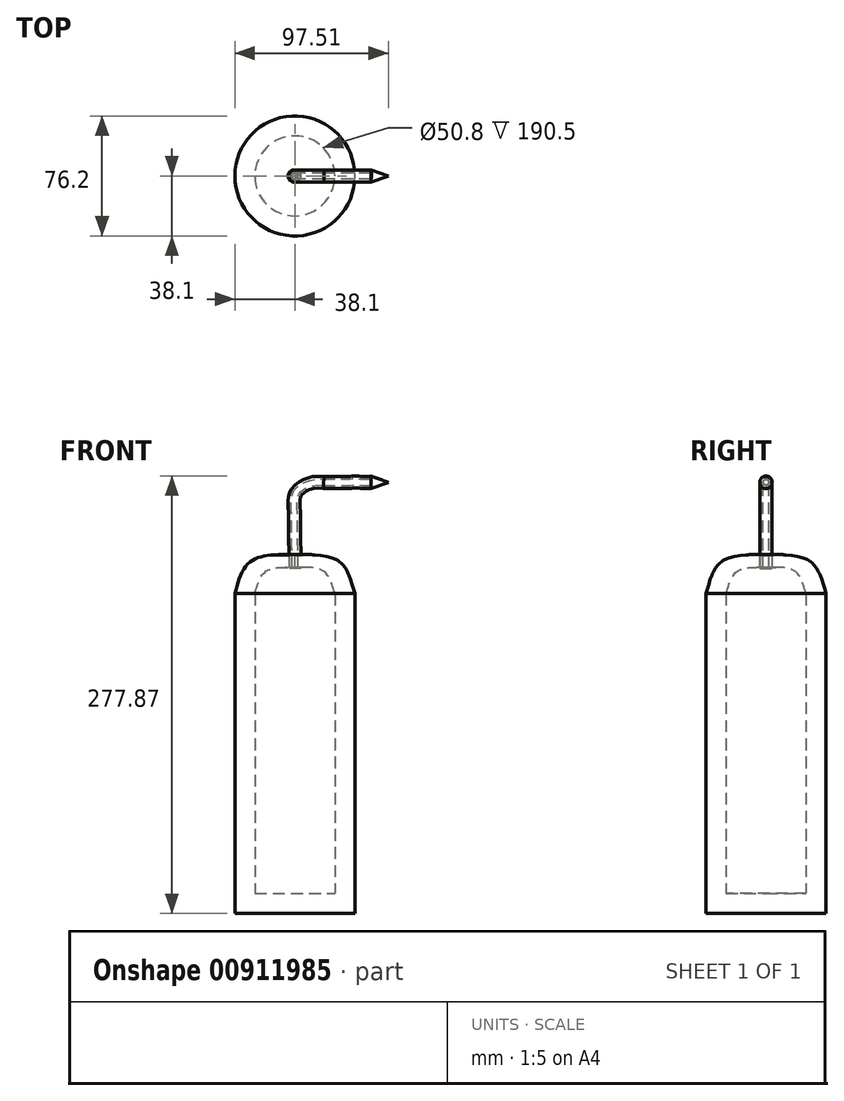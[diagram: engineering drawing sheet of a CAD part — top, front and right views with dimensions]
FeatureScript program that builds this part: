
annotation { "Feature Type Name" : "Feature", "Feature Type Description" : "" }
export const myFeature = defineFeature(function(context is Context, id is Id, definition is map)
    precondition{}
    {
        {
            var Q0;
            Q0=qCreatedBy(makeId("Front.planeOp"),FACE);
            var sketch = newSketch(context, id + "F0", { "sketchPlane" : qUnion([Q0])});
            skLineSegment(sketch, "E0.bottom", {"start": v(-34.29, 171.4) * mm, "end": v(-21.59, 171.4) * mm});
            skLineSegment(sketch, "E0.top", {"start": v(-34.29, -31.8) * mm, "end": v(-21.59, -31.8) * mm});
            skLineSegment(sketch, "E0.left", {"start": v(-34.29, 171.4) * mm, "end": v(-34.29, -31.8) * mm});
            skLineSegment(sketch, "E0.right", {"start": v(-21.59, 171.4) * mm, "end": v(-21.59, -31.8) * mm});
            skLineSegment(sketch, "E1.bottom", {"start": v(-21.59, -19.1) * mm, "end": v(3.81, -19.1) * mm});
            skLineSegment(sketch, "E1.top", {"start": v(-21.59, -31.8) * mm, "end": v(3.81, -31.8) * mm});
            skLineSegment(sketch, "E1.left", {"start": v(-21.59, -19.1) * mm, "end": v(-21.59, -31.8) * mm});
            skLineSegment(sketch, "E1.right", {"start": v(3.81, -19.1) * mm, "end": v(3.81, -31.8) * mm});
            skLineSegment(sketch, "E2", {"start": v(3.81, -19.1) * mm, "end": v(3.81, 201.68) * mm, "construction": true});
            skLineSegment(sketch, "E3", {"start": v(-21.59, 171.4) * mm, "end": v(3.81, 171.4) * mm, "construction": true});
            skLineSegment(sketch, "E4", {"start": v(0, 171.4) * mm, "end": v(0, 200.93) * mm, "construction": true});
            skLineSegment(sketch, "E5", {"start": v(0, 171.4) * mm, "end": v(3.81, 171.4) * mm, "construction": true});
            skFitSpline(sketch, "E6", {"points": [v(-21.59, 171.4) * mm, v(-14.67, 185.45) * mm, v(0, 188.03) * mm], "startDerivative": vector(9.61, 33.45) * mm, "endDerivative": vector(33.67, -0.32) * mm});
            skFitSpline(sketch, "E7", {"points": [v(-34.29, 171.4) * mm, v(-26.66, 189.62) * mm, v(-14.36, 195.48) * mm, v(0, 195.64) * mm], "startDerivative": vector(14.37, 54.55) * mm, "endDerivative": vector(38.3, -6.03) * mm});
            skLineSegment(sketch, "E8", {"start": v(0, 195.64) * mm, "end": v(0, 188.03) * mm});
            skSolve(sketch);
        }
        {
            var Q0;
            Q0=qCreatedBy(makeId("Front.planeOp"),FACE);
            var sketch = newSketch(context, id + "F1", { "sketchPlane" : qUnion([Q0])});
            skFitSpline(sketch, "E9", {"points": [v(3.99, 187.38) * mm, v(3.66, 212.53) * mm, v(3.53, 222.24) * mm, v(3.38, 230.4) * mm, v(5.65, 236.87) * mm, v(22.13, 242.12) * mm], "startDerivative": vector(-1.45, 96.27) * mm, "endDerivative": vector(99.72, -10.55) * mm});
            skFitSpline(sketch, "E10", {"points": [v(22.13, 242.12) * mm, v(38.2, 242.12) * mm, v(48.37, 242.12) * mm, v(52.5, 242.12) * mm], "startDerivative": vector(40.87, -1.49) * mm, "endDerivative": vector(16.8, 0) * mm});
            skFitSpline(sketch, "E11", {"points": [v(52.5, 242.12) * mm, v(58, 242.12) * mm], "startDerivative": vector(5.5, 0) * mm, "endDerivative": vector(5.5, 0) * mm});
            skLineSegment(sketch, "E12", {"start": v(58, 242.12) * mm, "end": v(58, -57.55) * mm, "construction": true});
            skSolve(sketch);
        }
        {
            var Q0;
            Q0=sQuery(id+"F1.wireOp",VERTEX,"E9.start");
            var Q1;
            Q1=sQuery(id+"F1.wireOp",EDGE,"E9");
            cPlane(context, id + "F2", {"entities" : qUnion([Q0, Q1]), "cplaneType" : CPlaneType.CURVE_POINT, "offset" : 25.4 * mm, "width" : 152.4 * mm, "height" : 152.4 * mm});
        }
        {
            var Q0;
            Q0=qCreatedBy(id+"F2.planeOp",FACE);
            var sketch = newSketch(context, id + "F3", { "sketchPlane" : qUnion([Q0])});
            skCircle(sketch, "E13", {"center": v(6.8, 0) * mm, "radius": 3.8 * mm});
            skCircle(sketch, "E14", {"center": v(6.8, 0) * mm, "radius": 1.9 * mm});
            skSolve(sketch);
        }
        {
            var Q0;
            {var subQ2=sQuery(id+"F0.wireOp",EDGE,"E0.bottom");var subQ3=sQuery(id+"F0.wireOp",EDGE,"E1.bottom");var subQ6=makeQuery(id+"F0.imprint","IMPRINT",EDGE,{"derivedFrom":subQ2});Q0=qUnion([makeQuery(id+"F0.imprint","IMPRINT",FACE,{"disambiguationData":[TD([[subQ6,1.0]])]}),makeQuery(id+"F0.imprint","IMPRINT",FACE,{"disambiguationData":[TD([[makeQuery(id+"F0.imprint","IMPRINT",EDGE,{"derivedFrom":subQ3}),-1.0]])]}),makeQuery(id+"F0.imprint","IMPRINT",FACE,{"disambiguationData":[TD([[subQ6,-1.0]])]})]);}
            var Q1;
            Q1=sQuery(id+"F0.wireOp",EDGE,"E2");
            revolve(context, id + "F4", {"surfaceOperationType" : NewSurfaceOperationType.NEW, "entities" : qUnion([Q0]), "axis" : qUnion([Q1]), "revolveType" : RevolveType.FULL});
        }
        {
            var Q0;
            Q0 = qSketchRegion(id + "F3", true);
            var Q1;
            Q1=sQuery(id+"F1.wireOp",EDGE,"E9");
            var Q2;
            Q2=sQuery(id+"F1.wireOp",EDGE,"E10");
            sweep(context, id + "F5", {"operationType" : NewBodyOperationType.ADD, "profiles" : qUnion([Q0]), "path" : qUnion([Q1, Q2])});
        }
        {
            var Q0;
            Q0=qCreatedBy(makeId("Top.planeOp"),FACE);
            cPlane(context, id + "F6", {"entities" : qUnion([Q0]), "cplaneType" : CPlaneType.OFFSET, "offset" : 242.06 * mm, "width" : 152.4 * mm, "height" : 152.4 * mm});
        }
        {
            var Q0;
            Q0=qCreatedBy(id+"F6.planeOp",FACE);
            var sketch = newSketch(context, id + "F7", { "sketchPlane" : qUnion([Q0])});
            skLineSegment(sketch, "E15", {"start": v(52.2, -0.05) * mm, "end": v(63.22, -0.05) * mm});
            skLineSegment(sketch, "E16", {"start": v(52.2, -0.05) * mm, "end": v(52.2, -4) * mm});
            skLineSegment(sketch, "E17", {"start": v(52.2, -4) * mm, "end": v(63.22, -0.05) * mm});
            skSolve(sketch);
        }
        {
            var Q0;
            Q0 = qSketchRegion(id + "F7", true);
            var Q1;
            Q1=sQuery(id+"F7.wireOp",EDGE,"E15");
            revolve(context, id + "F8", {"operationType" : NewBodyOperationType.ADD, "surfaceOperationType" : NewSurfaceOperationType.NEW, "entities" : qUnion([Q0]), "axis" : qUnion([Q1]), "revolveType" : RevolveType.FULL});
        }
    });
